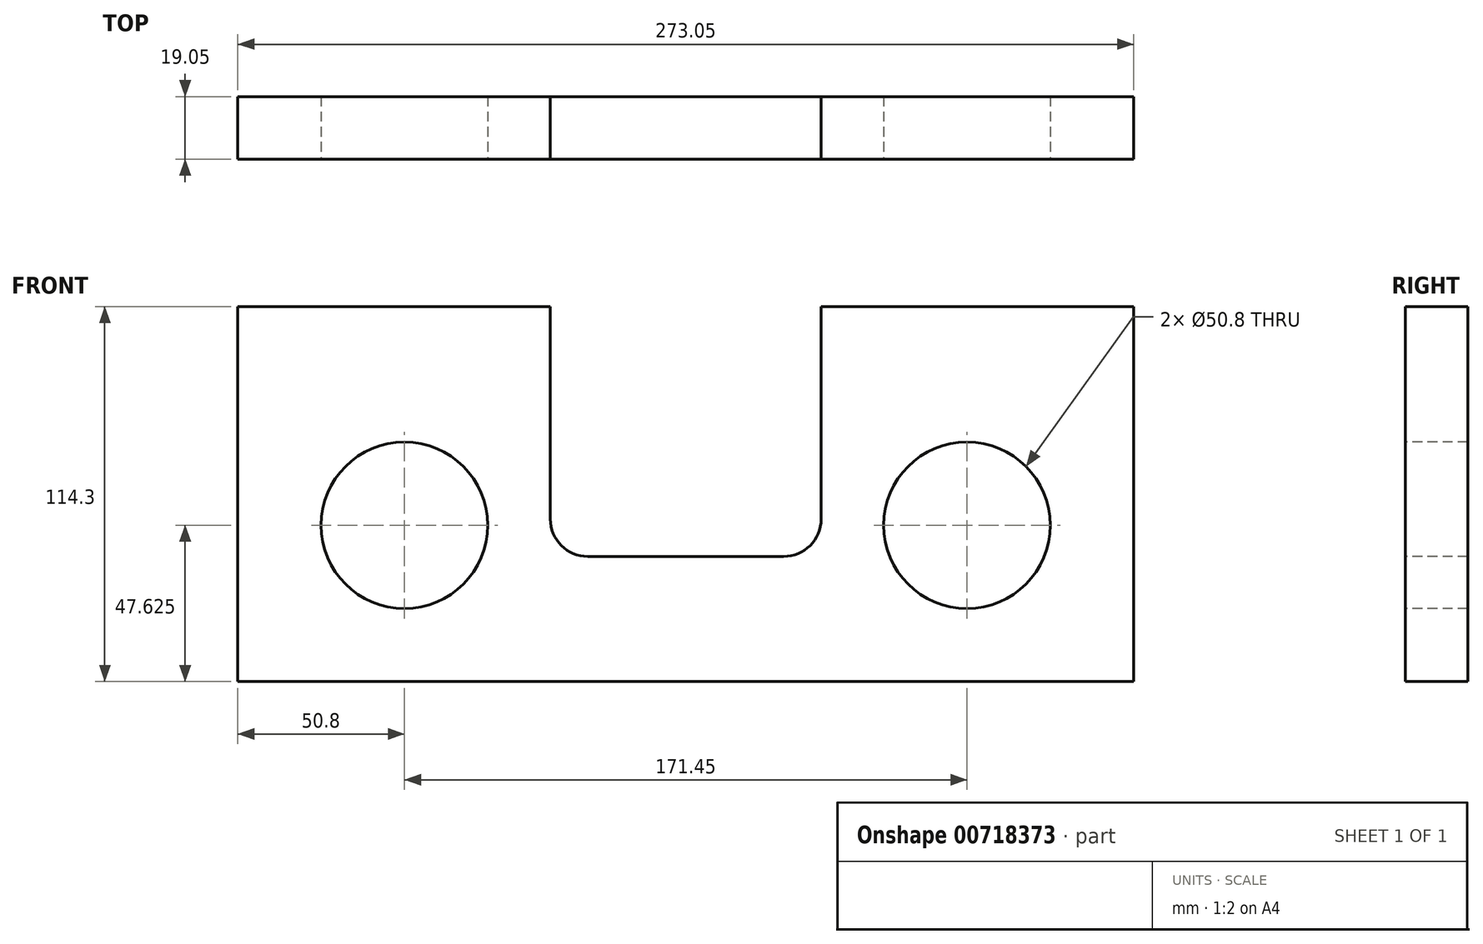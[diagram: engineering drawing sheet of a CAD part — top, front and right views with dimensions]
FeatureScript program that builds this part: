
annotation { "Feature Type Name" : "Feature", "Feature Type Description" : "" }
export const myFeature = defineFeature(function(context is Context, id is Id, definition is map)
    precondition{}
    {
        {
            var Q0;
            Q0=qCreatedBy(makeId("Front.planeOp"),FACE);
            var sketch = newSketch(context, id + "F0", { "sketchPlane" : qUnion([Q0])});
            skLineSegment(sketch, "E0.bottom", {"start": v(0, 0) * mm, "end": v(273.05, 0) * mm});
            skLineSegment(sketch, "E0.top", {"start": v(0, 114.3) * mm, "end": v(273.05, 114.3) * mm});
            skLineSegment(sketch, "E0.left", {"start": v(0, 0) * mm, "end": v(0, 114.3) * mm});
            skLineSegment(sketch, "E0.right", {"start": v(273.05, 0) * mm, "end": v(273.05, 114.3) * mm});
            skSolve(sketch);
        }
        {
            var Q0;
            Q0 = qSketchRegion(id + "F0", true);
            extrude(context, id + "F1", {"entities" : qUnion([Q0]), "depth" : 19.05 * mm, "offsetDistance" : 25.4 * mm});
        }
        {
            var Q0;
            Q0=makeQuery(id+"F1.opExtrude","CAP_FACE",FACE,{"disambiguationData":[OSD([sQuery(id+"F0.wireOp",EDGE,"E0.bottom"),sQuery(id+"F0.wireOp",EDGE,"E0.top"),sQuery(id+"F0.wireOp",EDGE,"E0.left"),sQuery(id+"F0.wireOp",EDGE,"E0.right")])],"isStart":false});
            var sketch = newSketch(context, id + "F2", { "sketchPlane" : qUnion([Q0])});
            skCircle(sketch, "E1", {"center": v(50.8, 47.63) * mm, "radius": 25.4 * mm});
            skCircle(sketch, "E2", {"center": v(222.25, 47.63) * mm, "radius": 25.4 * mm});
            skSolve(sketch);
        }
        {
            var Q0;
            Q0=makeQuery(id+"F2.imprint","IMPRINT",FACE,{"disambiguationData":[TD([[makeQuery(id+"F2.imprint","IMPRINT",EDGE,{"derivedFrom":sQuery(id+"F2.wireOp",EDGE,"E2")}),1.0]])]});
            var Q1;
            Q1=makeQuery(id+"F2.imprint","IMPRINT",FACE,{"disambiguationData":[TD([[makeQuery(id+"F2.imprint","IMPRINT",EDGE,{"derivedFrom":sQuery(id+"F2.wireOp",EDGE,"E1")}),1.0]])]});
            extrude(context, id + "F3", {"entities" : qUnion([Q0, Q1]), "operationType" : NewBodyOperationType.REMOVE, "oppositeDirection" : true, "depth" : 25.4 * mm, "offsetDistance" : 25.4 * mm});
        }
        {
            var Q0;
            Q0=makeQuery(id+"F1.opExtrude","CAP_FACE",FACE,{"disambiguationData":[OSD([sQuery(id+"F0.wireOp",EDGE,"E0.bottom"),sQuery(id+"F0.wireOp",EDGE,"E0.top"),sQuery(id+"F0.wireOp",EDGE,"E0.left"),sQuery(id+"F0.wireOp",EDGE,"E0.right")])],"isStart":false});
            var sketch = newSketch(context, id + "F4", { "sketchPlane" : qUnion([Q0])});
            skLineSegment(sketch, "E3", {"start": v(95.25, 114.3) * mm, "end": v(95.25, 49.53) * mm});
            skLineSegment(sketch, "E4", {"start": v(106.68, 38.1) * mm, "end": v(166.37, 38.1) * mm});
            skLineSegment(sketch, "E5", {"start": v(177.8, 49.53) * mm, "end": v(177.8, 114.3) * mm});
            skPoint(sketch, "E6.visualSharp", {"position": v(95.25, 38.1) * mm});
            skArc(sketch, "E6.filletArc", {"start": v(95.25, 49.53) * mm, "mid": v(98.6, 41.45) * mm, "end": v(106.68, 38.1) * mm});
            skPoint(sketch, "E7.visualSharp", {"position": v(177.8, 38.1) * mm});
            skArc(sketch, "E7.filletArc", {"start": v(166.37, 38.1) * mm, "mid": v(174.45, 41.45) * mm, "end": v(177.8, 49.53) * mm});
            skSolve(sketch);
        }
        {
            var Q0;
            {var subQ1=sQuery(id+"F4.wireOp",EDGE,"E3");Q0=makeQuery(id+"F4.imprint","IMPRINT",FACE,{"disambiguationData":[TD([[makeQuery(id+"F4.imprint","IMPRINT",EDGE,{"derivedFrom":subQ1}),1.0]])]});}
            extrude(context, id + "F5", {"entities" : qUnion([Q0]), "operationType" : NewBodyOperationType.REMOVE, "oppositeDirection" : true, "depth" : 25.4 * mm, "offsetDistance" : 25.4 * mm});
        }
    });
